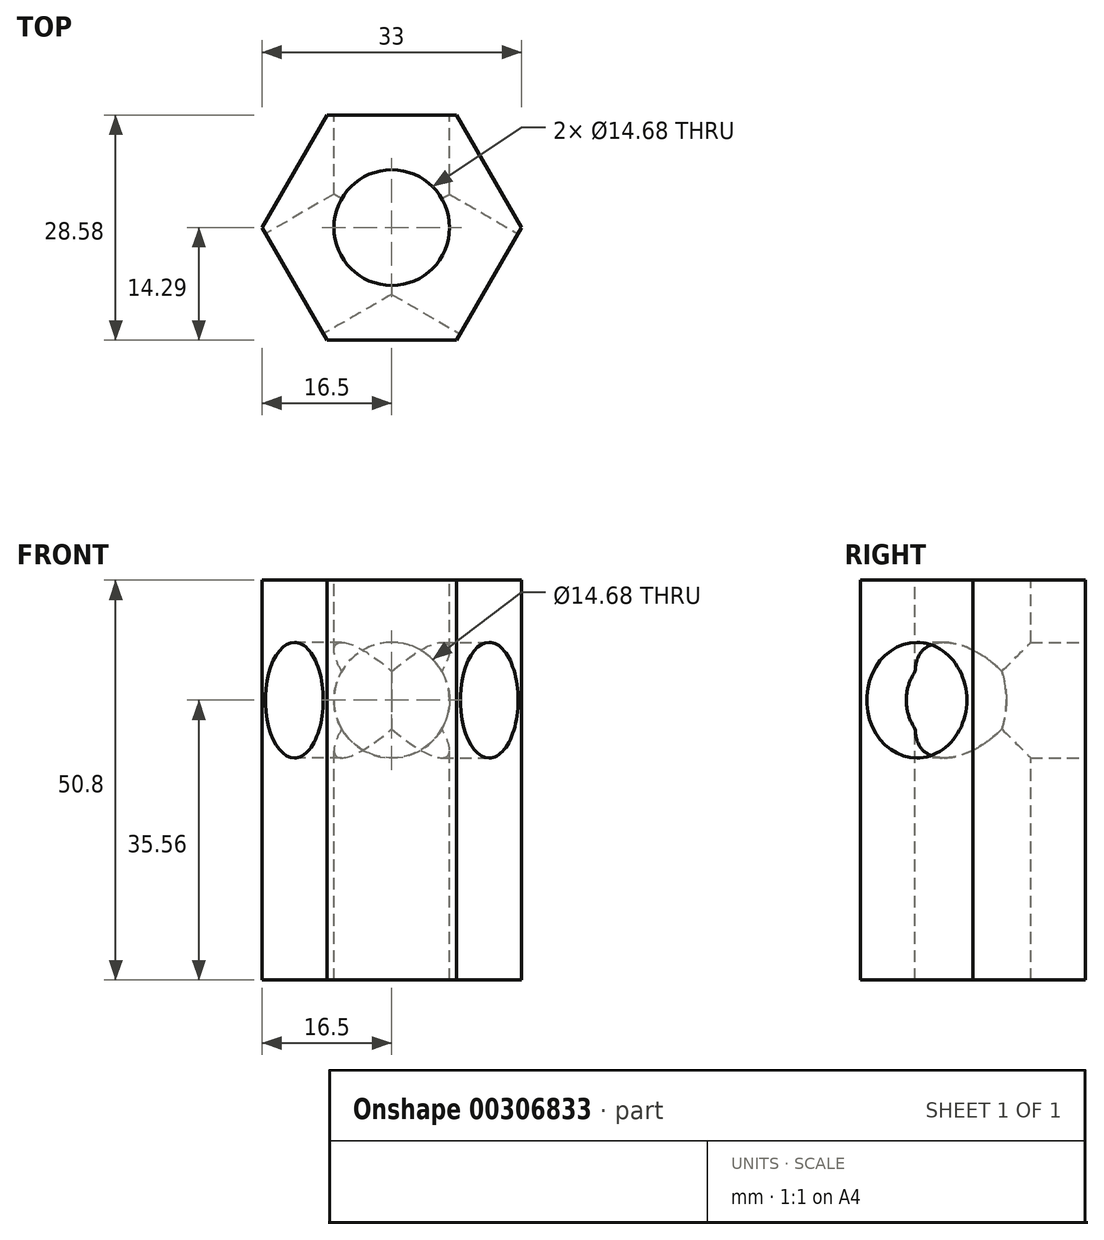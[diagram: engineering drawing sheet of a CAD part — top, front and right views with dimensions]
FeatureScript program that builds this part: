
annotation { "Feature Type Name" : "Feature", "Feature Type Description" : "" }
export const myFeature = defineFeature(function(context is Context, id is Id, definition is map)
    precondition{}
    {
        {
            var Q0;
            Q0=qCreatedBy(makeId("Top.planeOp"),FACE);
            var sketch = newSketch(context, id + "F0", { "sketchPlane" : qUnion([Q0])});
            skCircle(sketch, "E0.cCircle", {"center": v(0, 0) * mm, "radius": 14.29 * mm, "construction": true});
            skLineSegment(sketch, "E0.0", {"start": v(-8.25, 14.29) * mm, "end": v(8.25, 14.29) * mm});
            skLineSegment(sketch, "E0.1", {"start": v(8.25, 14.29) * mm, "end": v(16.5, 0) * mm});
            skLineSegment(sketch, "E0.2", {"start": v(16.5, 0) * mm, "end": v(8.25, -14.29) * mm});
            skLineSegment(sketch, "E0.3", {"start": v(8.25, -14.29) * mm, "end": v(-8.25, -14.29) * mm});
            skLineSegment(sketch, "E0.4", {"start": v(-8.25, -14.29) * mm, "end": v(-16.5, 0) * mm});
            skLineSegment(sketch, "E0.5", {"start": v(-16.5, 0) * mm, "end": v(-8.25, 14.29) * mm});
            skPoint(sketch, "E0.0.midPoint", {"position": v(0, 14.29) * mm});
            skCircle(sketch, "E1", {"center": v(0, 0) * mm, "radius": 7.34 * mm});
            skSolve(sketch);
        }
        {
            var Q0;
            Q0=makeQuery(id+"F0.imprint","IMPRINT",FACE,{"disambiguationData":[TD([[makeQuery(id+"F0.imprint","IMPRINT",EDGE,{"derivedFrom":sQuery(id+"F0.wireOp",EDGE,"E0.0")}),-1.0]])]});
            extrude(context, id + "F1", {"entities" : qUnion([Q0]), "endBound" : BoundingType.SYMMETRIC, "oppositeDirection" : true, "depth" : 50.8 * mm});
        }
        {
            var Q0;
            Q0=makeQuery(id+"F1.opExtrude","SWEPT_FACE",FACE,{"disambiguationData":[OSD([sQuery(id+"F0.wireOp",EDGE,"E0.2")])]});
            var sketch = newSketch(context, id + "F2", { "sketchPlane" : qUnion([Q0])});
            skCircle(sketch, "E2", {"center": v(0, 10.16) * mm, "radius": 7.34 * mm});
            skSolve(sketch);
        }
        {
            var Q0;
            Q0=makeQuery(id+"F1.opExtrude","SWEPT_FACE",FACE,{"disambiguationData":[OSD([sQuery(id+"F0.wireOp",EDGE,"E0.0")])]});
            var sketch = newSketch(context, id + "F3", { "sketchPlane" : qUnion([Q0])});
            skCircle(sketch, "E3", {"center": v(0, 10.16) * mm, "radius": 7.34 * mm});
            skSolve(sketch);
        }
        {
            var Q0;
            Q0=makeQuery(id+"F1.opExtrude","SWEPT_FACE",FACE,{"disambiguationData":[OSD([sQuery(id+"F0.wireOp",EDGE,"E0.4")])]});
            var sketch = newSketch(context, id + "F4", { "sketchPlane" : qUnion([Q0])});
            skCircle(sketch, "E4", {"center": v(0, 10.16) * mm, "radius": 7.34 * mm});
            skSolve(sketch);
        }
        {
            var Q0;
            Q0=sQuery(id+"F3.wireOp",VERTEX,"E3.center");
            var Q1;
            Q1=sQuery(id+"F2.wireOp",VERTEX,"E2.center");
            var Q2;
            Q2=sQuery(id+"F4.wireOp",VERTEX,"E4.center");
            var Q3;
            Q3=makeQuery(id+"F1.opExtrude","SWEPT_BODY",BODY,{"disambiguationData":[OSD([sQuery(id+"F0.wireOp",EDGE,"E0.0"),sQuery(id+"F0.wireOp",EDGE,"E0.1"),sQuery(id+"F0.wireOp",EDGE,"E0.2"),sQuery(id+"F0.wireOp",EDGE,"E0.3"),sQuery(id+"F0.wireOp",EDGE,"E0.4"),sQuery(id+"F0.wireOp",EDGE,"E0.5"),sQuery(id+"F0.wireOp",EDGE,"E1")])]});
            hole(context, id + "F5", {"style" : HoleStyle.SIMPLE, "endStyle" : HoleEndStyle.BLIND, "holeDiameter" : 14.68 * mm, "holeDepth" : 16.5 * mm, "tappedDepth" : 12.7 * mm, "tapClearance" : 3, "startFromSketch" : true, "locations" : qUnion([Q0, Q1, Q2]), "scope" : qUnion([Q3])});
        }
    });
